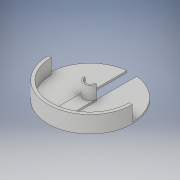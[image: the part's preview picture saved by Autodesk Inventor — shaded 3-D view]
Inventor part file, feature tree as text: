
AUTODESK INVENTOR PART (.ipt)
format: ipt  version: 2017 (Build 210142000, 142)  size: 142,848 bytes
history: native  units: in
note: dims shown in document units (in); Inventor stores cm internally (conversion verified against a paired STEP export)
features: extrude x6, sketch x6
ambient origin geometry x8: Origin, YZ Plane, XZ Plane, XY Plane, X Axis, Y Axis, Z Axis, Center Point
bodies: Solid1 (feature_tree)
feature tree (12):
  extrude  "Extrusion1"  Depth=1.1024in TaperAngle=0.0deg
  extrude  "Extrusion2"  Depth=1.1024in TaperAngle=0.0deg
  extrude  "Extrusion3"  Depth=0.9843in TaperAngle=0.0deg
  extrude  "Extrusion4"  Depth=0.6496in
  extrude  "Extrusion5"  [1 undecoded]
  extrude  "Extrusion6"  [1 undecoded]
  sketch  "Sketch1"  dims[d0=5.5118in d1=1.1024in d2=0.0in]
  sketch  "Sketch2"  dims[d3=0.6496in d4=1.1024in d5=0.0in]
  sketch  "Sketch3"  dims[d6=5.1181in d7=0.8268in d8=0.9843in d9=0.0in d10=8.6614in d11=0.0in]
  sketch  "Sketch4"  dims[d12=0.1181in d13=0.0in d14=0.6496in]
  sketch  "Sketch5"  dims[d15=1.1811in d16=0.0in]
  sketch  "Sketch6"
note: 2 required parameter values undecoded (feature->parameter linkage not recoverable at this tier; creation-order binding heuristic only, values carry confidence <= 0.55)
